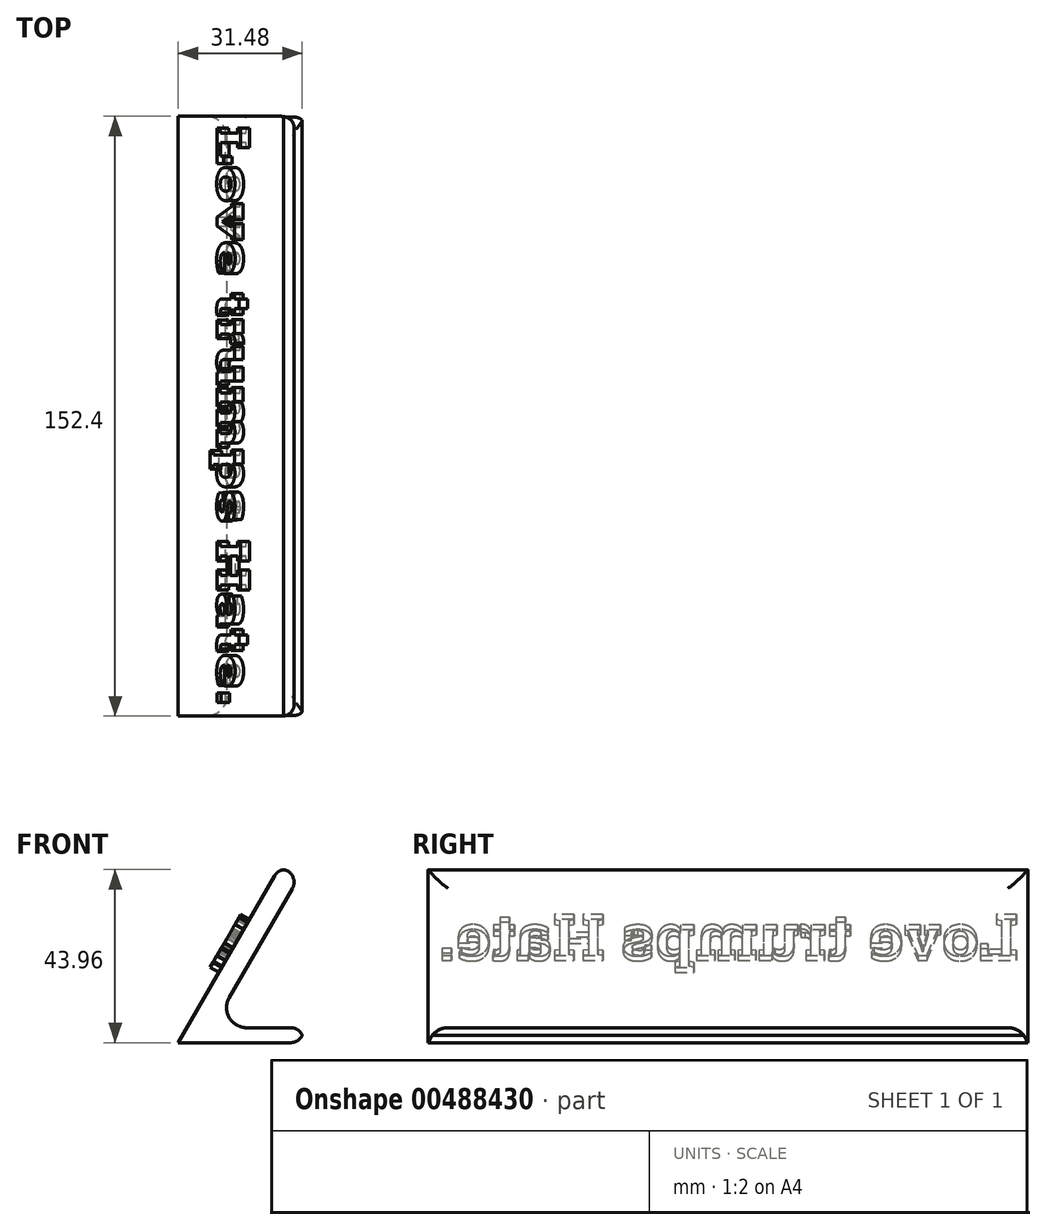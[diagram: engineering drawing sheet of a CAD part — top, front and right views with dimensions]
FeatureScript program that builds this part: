
annotation { "Feature Type Name" : "Feature", "Feature Type Description" : "" }
export const myFeature = defineFeature(function(context is Context, id is Id, definition is map)
    precondition{}
    {
        {
            var Q0;
            Q0=qCreatedBy(makeId("Front.planeOp"),FACE);
            var sketch = newSketch(context, id + "F0", { "sketchPlane" : qUnion([Q0])});
            skLineSegment(sketch, "E0", {"start": v(0, 44) * mm, "end": v(-23.2, 3.8) * mm});
            skLineSegment(sketch, "E1", {"start": v(-23.2, 3.8) * mm, "end": v(0, 3.8) * mm});
            skLineSegment(sketch, "E2", {"start": v(0, 3.8) * mm, "end": v(0, 0) * mm});
            skLineSegment(sketch, "E3", {"start": v(0, 0) * mm, "end": v(-31.75, 0) * mm});
            skLineSegment(sketch, "E4", {"start": v(-31.75, 0) * mm, "end": v(-6.35, 44) * mm});
            skLineSegment(sketch, "E5", {"start": v(-6.35, 44) * mm, "end": v(0, 44) * mm});
            skSolve(sketch);
        }
        {
            var Q0;
            Q0 = qSketchRegion(id + "F0", true);
            extrude(context, id + "F1", {"entities" : qUnion([Q0]), "depth" : 152.4 * mm});
        }
        {
            var Q0;
            Q0=makeQuery(id+"F1.opExtrude","SWEPT_EDGE",EDGE,{"disambiguationData":[OSD([sQuery(id+"F0.wireOp",EDGE,"E4"),sQuery(id+"F0.wireOp",EDGE,"E5")])]});
            var Q1;
            Q1=makeQuery(id+"F1.opExtrude","SWEPT_EDGE",EDGE,{"disambiguationData":[OSD([sQuery(id+"F0.wireOp",EDGE,"E0"),sQuery(id+"F0.wireOp",EDGE,"E5")])]});
            var Q2;
            Q2=makeQuery(id+"F1.opExtrude","SWEPT_EDGE",EDGE,{"disambiguationData":[OSD([sQuery(id+"F0.wireOp",EDGE,"E1"),sQuery(id+"F0.wireOp",EDGE,"E2")])]});
            var Q3;
            Q3=makeQuery(id+"F1.opExtrude","SWEPT_EDGE",EDGE,{"disambiguationData":[OSD([sQuery(id+"F0.wireOp",EDGE,"E2"),sQuery(id+"F0.wireOp",EDGE,"E3")])]});
            fillet(context, id + "F2", {"entities" : qUnion([Q0, Q1, Q2, Q3]), "radius" : 3.17 * mm, "tangentPropagation" : true, "allowEdgeOverflow" : false});
        }
        {
            var Q0;
            Q0=makeQuery(id+"F1.opExtrude","SWEPT_EDGE",EDGE,{"disambiguationData":[OSD([sQuery(id+"F0.wireOp",EDGE,"E0"),sQuery(id+"F0.wireOp",EDGE,"E1")])]});
            fillet(context, id + "F3", {"entities" : qUnion([Q0]), "radius" : 5.08 * mm, "tangentPropagation" : true, "allowEdgeOverflow" : false});
        }
        {
            var Q0;
            Q0=makeQuery(id+"F1.opExtrude","CAP_EDGE",EDGE,{"disambiguationData":[OSD([sQuery(id+"F0.wireOp",EDGE,"E0")])],"isStart":false});
            var Q1;
            Q1=makeQuery(id+"F1.opExtrude","CAP_EDGE",EDGE,{"disambiguationData":[OSD([sQuery(id+"F0.wireOp",EDGE,"E0")])],"isStart":true});
            fillet(context, id + "F4", {"entities" : qUnion([Q0, Q1]), "radius" : 5.08 * mm, "tangentPropagation" : true, "allowEdgeOverflow" : false});
        }
        {
            var Q0;
            Q0=makeQuery(id+"F1.opExtrude","SWEPT_FACE",FACE,{"disambiguationData":[OSD([sQuery(id+"F0.wireOp",EDGE,"E4")])]});
            var sketch = newSketch(context, id + "F5", { "sketchPlane" : qUnion([Q0])});
            skText(sketch, "E6", { "text": "Love trumps Hate.", "fontName": "RobotoSlab-Bold.ttf"});
            const initialGuessF5  = {"E6": [0.00254, 0.00822, 1, 0, 0.01218]};
            skSetInitialGuess(sketch, initialGuessF5);
            skSolve(sketch);
        }
        {
            var Q0;
            Q0 = qSketchRegion(id + "F5", true);
            extrude(context, id + "F6", {"entities" : qUnion([Q0]), "operationType" : NewBodyOperationType.ADD, "depth" : 2.54 * mm});
        }
    });
